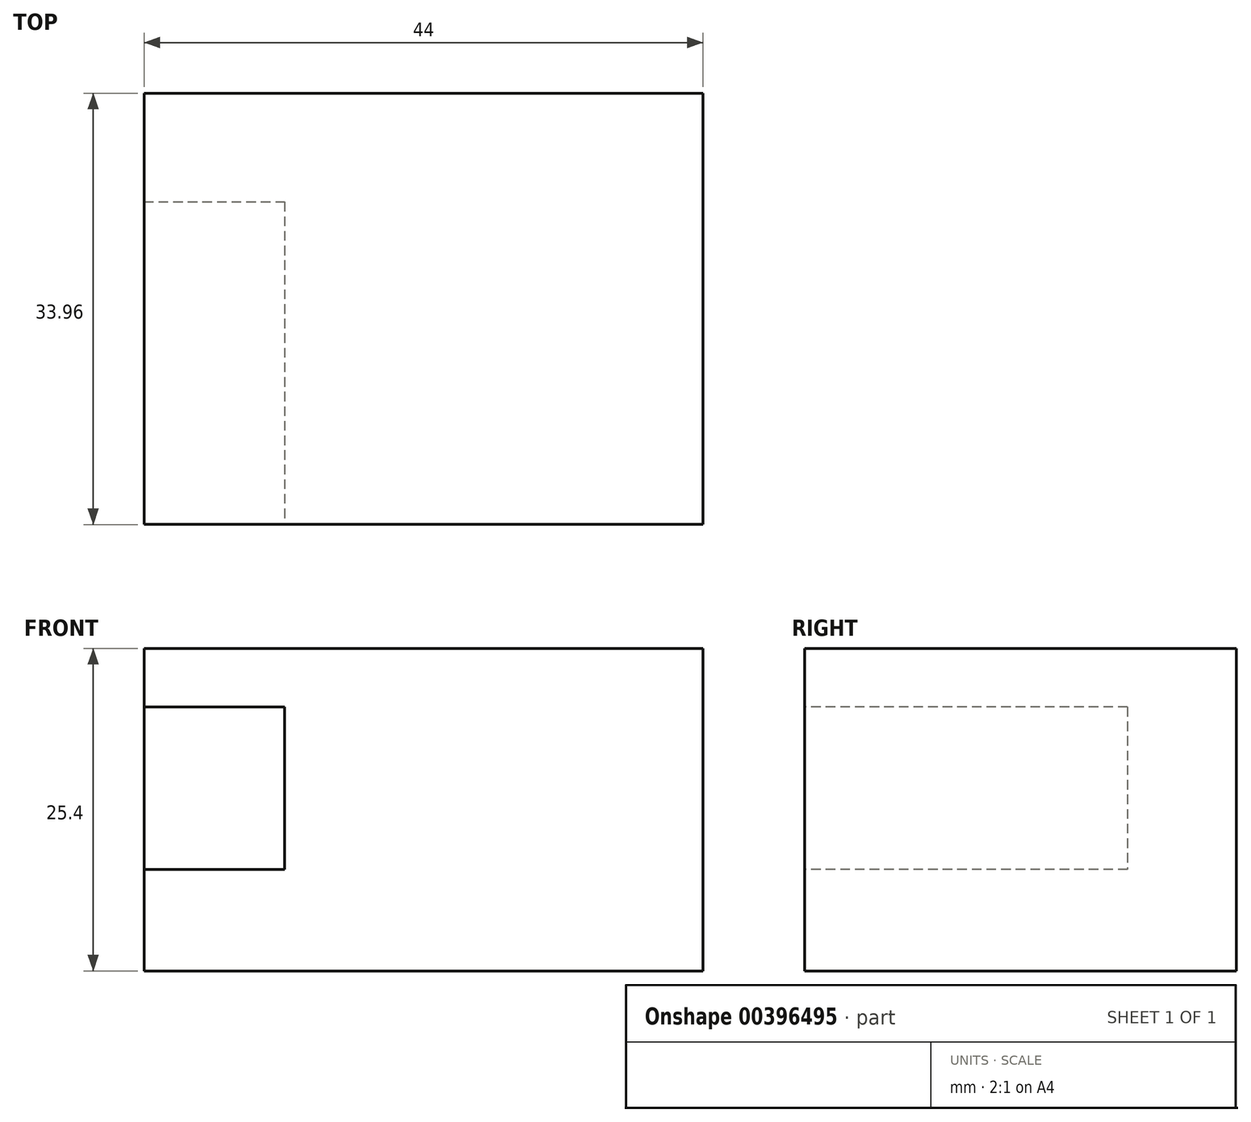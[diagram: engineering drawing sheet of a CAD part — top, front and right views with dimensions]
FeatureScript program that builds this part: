
annotation { "Feature Type Name" : "Feature", "Feature Type Description" : "" }
export const myFeature = defineFeature(function(context is Context, id is Id, definition is map)
    precondition{}
    {
        {
            var Q0;
            Q0=qCreatedBy(makeId("Top.planeOp"),FACE);
            var sketch = newSketch(context, id + "F0", { "sketchPlane" : qUnion([Q0])});
            skLineSegment(sketch, "E0.bottom", {"start": v(0, 0) * mm, "end": v(44, 0) * mm});
            skLineSegment(sketch, "E0.top", {"start": v(0, -33.96) * mm, "end": v(44, -33.96) * mm});
            skLineSegment(sketch, "E0.left", {"start": v(0, 0) * mm, "end": v(0, -33.96) * mm});
            skLineSegment(sketch, "E0.right", {"start": v(44, 0) * mm, "end": v(44, -33.96) * mm});
            skSolve(sketch);
        }
        {
            var Q0;
            Q0=makeQuery(id+"F0.imprint","IMPRINT",FACE,{"disambiguationData":[TD([[makeQuery(id+"F0.imprint","IMPRINT",EDGE,{"derivedFrom":sQuery(id+"F0.wireOp",EDGE,"E0.bottom")}),-1.0]])]});
            extrude(context, id + "F1", {"entities" : qUnion([Q0]), "depth" : 25.4 * mm});
        }
        {
            var Q0;
            Q0=makeQuery(id+"F1.opExtrude","SWEPT_FACE",FACE,{"disambiguationData":[OSD([sQuery(id+"F0.wireOp",EDGE,"E0.top")])]});
            var sketch = newSketch(context, id + "F2", { "sketchPlane" : qUnion([Q0])});
            skLineSegment(sketch, "E1.bottom", {"start": v(-17.8, 20.78) * mm, "end": v(11.07, 20.78) * mm});
            skLineSegment(sketch, "E1.top", {"start": v(-17.8, 7.98) * mm, "end": v(11.07, 7.98) * mm});
            skLineSegment(sketch, "E1.left", {"start": v(-17.8, 20.78) * mm, "end": v(-17.8, 7.98) * mm});
            skLineSegment(sketch, "E1.right", {"start": v(11.07, 20.78) * mm, "end": v(11.07, 7.98) * mm});
            skSolve(sketch);
        }
        {
            var Q0;
            {var subQ0=sQuery(id+"F2.wireOp",EDGE,"E1.right");Q0=makeQuery(id+"F2.imprint","IMPRINT",FACE,{"disambiguationData":[TD([[makeQuery(id+"F2.imprint","IMPRINT",EDGE,{"derivedFrom":subQ0}),-1.0]])]});}
            extrude(context, id + "F3", {"entities" : qUnion([Q0]), "operationType" : NewBodyOperationType.REMOVE, "oppositeDirection" : true, "depth" : 25.4 * mm});
        }
    });
